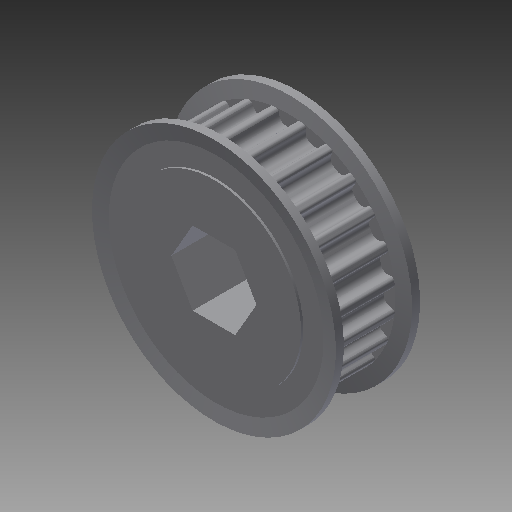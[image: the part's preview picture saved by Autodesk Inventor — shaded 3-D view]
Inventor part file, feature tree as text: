
AUTODESK INVENTOR PART (.ipt)
format: ipt  version: 2017 (Build 210142000, 142)  size: 921,600 bytes
history: native  units: in
note: dims shown in document units (in); Inventor stores cm internally (conversion verified against a paired STEP export)
features: mirror x1, other x1, imported_body x1
ambient origin geometry x8: Origin, YZ Plane, XZ Plane, XY Plane, X Axis, Y Axis, Z Axis, Center Point
bodies: Body1 (feature_tree)
feature tree (3):
  mirror  "Mirror1"
  other  "217-3227-STEP1"
  imported_body  "Base1"
